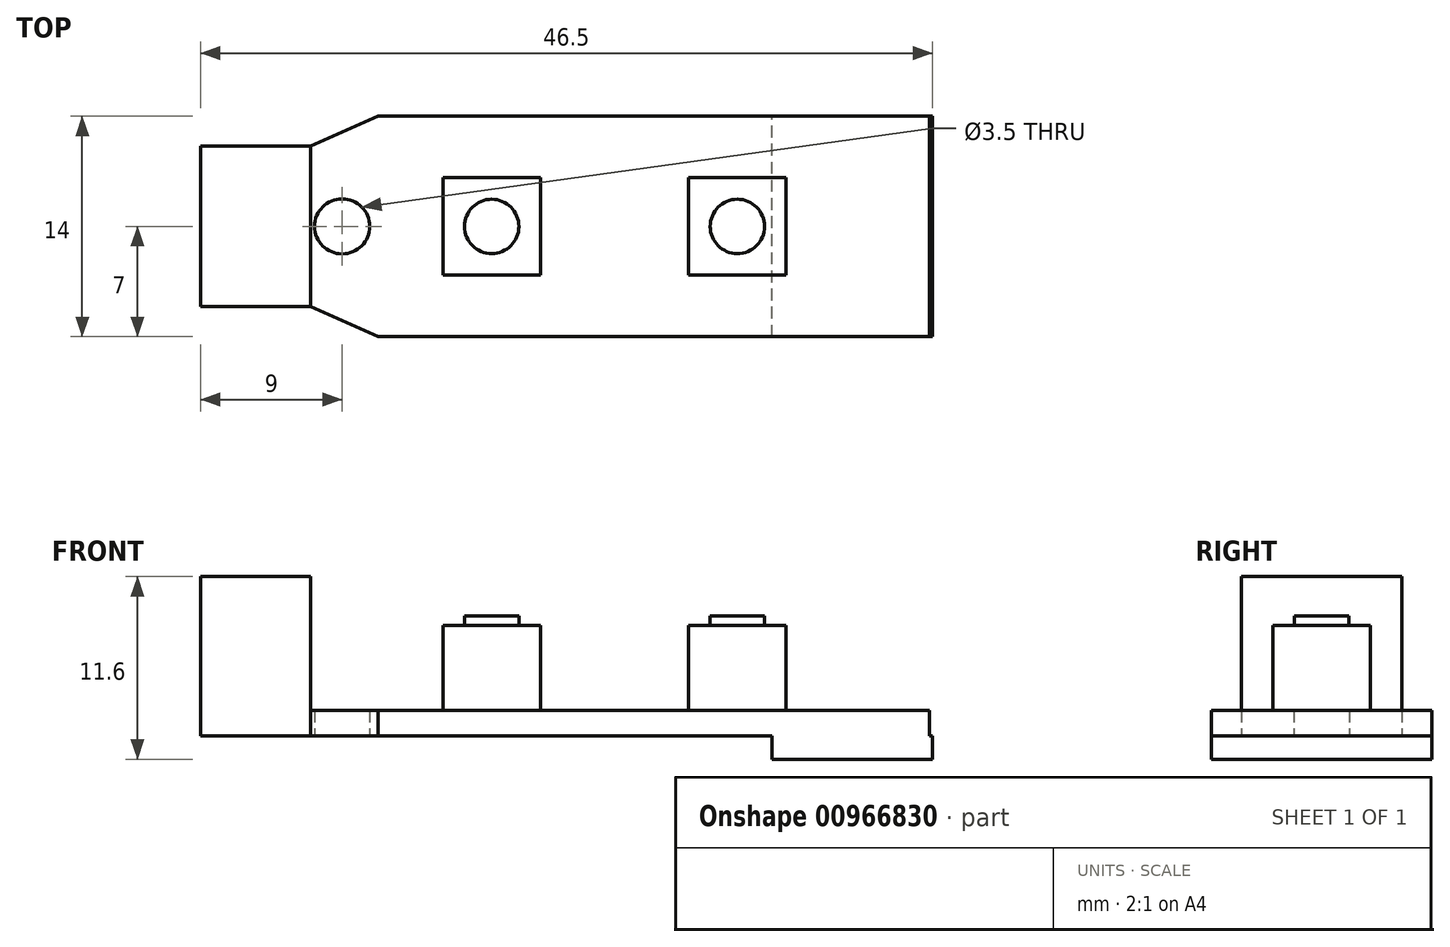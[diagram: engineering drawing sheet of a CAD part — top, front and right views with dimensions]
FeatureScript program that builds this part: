
annotation { "Feature Type Name" : "Feature", "Feature Type Description" : "" }
export const myFeature = defineFeature(function(context is Context, id is Id, definition is map)
    precondition{}
    {
        {
            var Q0;
            Q0=qCreatedBy(makeId("Top.planeOp"),FACE);
            var sketch = newSketch(context, id + "F0", { "sketchPlane" : qUnion([Q0])});
            skLineSegment(sketch, "E0.left", {"start": v(-23.15, 5.1) * mm, "end": v(-23.15, -5.1) * mm});
            skLineSegment(sketch, "E0.right", {"start": v(23.15, 7) * mm, "end": v(23.15, -7) * mm});
            skCircle(sketch, "E1", {"center": v(-14.15, 0) * mm, "radius": 1.75 * mm});
            skLineSegment(sketch, "E2", {"start": v(23.15, 7) * mm, "end": v(-11.85, 7) * mm});
            skLineSegment(sketch, "E3", {"start": v(23.15, -7) * mm, "end": v(-11.85, -7) * mm});
            skLineSegment(sketch, "E4", {"start": v(-23.15, 5.1) * mm, "end": v(-16.15, 5.1) * mm});
            skLineSegment(sketch, "E5", {"start": v(-23.15, -5.1) * mm, "end": v(-16.15, -5.1) * mm});
            skLineSegment(sketch, "E6", {"start": v(-16.15, 5.1) * mm, "end": v(-11.85, 7) * mm});
            skLineSegment(sketch, "E7", {"start": v(-16.15, -5.1) * mm, "end": v(-11.85, -7) * mm});
            skSolve(sketch);
        }
        {
            var Q0;
            Q0 = qSketchRegion(id + "F0", true);
            extrude(context, id + "F1", {"entities" : qUnion([Q0]), "depth" : 1.6 * mm, "offsetDistance" : 25 * mm});
        }
        {
            var Q0;
            Q0=makeQuery(id+"F1.opExtrude","CAP_FACE",FACE,{"disambiguationData":[OSD([sQuery(id+"F0.wireOp",EDGE,"E0.bottom"),sQuery(id+"F0.wireOp",EDGE,"E0.top"),sQuery(id+"F0.wireOp",EDGE,"E0.left"),sQuery(id+"F0.wireOp",EDGE,"E0.right"),sQuery(id+"F0.wireOp",EDGE,"E1")])],"isStart":false});
            var sketch = newSketch(context, id + "F2", { "sketchPlane" : qUnion([Q0])});
            skLineSegment(sketch, "E8.bottom", {"start": v(-23.15, 5.1) * mm, "end": v(-16.15, 5.1) * mm});
            skLineSegment(sketch, "E8.top", {"start": v(-23.15, -5.1) * mm, "end": v(-16.15, -5.1) * mm});
            skLineSegment(sketch, "E8.left", {"start": v(-23.15, 5.1) * mm, "end": v(-23.15, -5.1) * mm});
            skLineSegment(sketch, "E8.right", {"start": v(-16.15, 5.1) * mm, "end": v(-16.15, -5.1) * mm});
            skSolve(sketch);
        }
        {
            var Q0;
            Q0 = qSketchRegion(id + "F2", true);
            extrude(context, id + "F3", {"entities" : qUnion([Q0]), "operationType" : NewBodyOperationType.ADD, "depth" : 8.5 * mm, "offsetDistance" : 25 * mm});
        }
        {
            var Q0;
            Q0=makeQuery(id+"F1.opExtrude","CAP_FACE",FACE,{"disambiguationData":[OSD([sQuery(id+"F0.wireOp",EDGE,"E0.left"),sQuery(id+"F0.wireOp",EDGE,"E0.right"),sQuery(id+"F0.wireOp",EDGE,"E1"),sQuery(id+"F0.wireOp",EDGE,"E2"),sQuery(id+"F0.wireOp",EDGE,"E3"),sQuery(id+"F0.wireOp",EDGE,"JauPMEDd-Xxf6-qXM7-ZYm1-RprdkEthULBr"),sQuery(id+"F0.wireOp",EDGE,"BpJjFPcN-h0H7-t4R9-BkB2-neei3DgV5vJw")])],"isStart":false});
            var sketch = newSketch(context, id + "F4", { "sketchPlane" : qUnion([Q0])});
            skLineSegment(sketch, "E9.bottom", {"start": v(-7.75, 3.1) * mm, "end": v(-1.55, 3.1) * mm});
            skLineSegment(sketch, "E9.top", {"start": v(-7.75, -3.1) * mm, "end": v(-1.55, -3.1) * mm});
            skLineSegment(sketch, "E9.left", {"start": v(-7.75, 3.1) * mm, "end": v(-7.75, -3.1) * mm});
            skLineSegment(sketch, "E9.right", {"start": v(-1.55, 3.1) * mm, "end": v(-1.55, -3.1) * mm});
            skLineSegment(sketch, "E10.bottom", {"start": v(7.85, 3.1) * mm, "end": v(14.05, 3.1) * mm});
            skLineSegment(sketch, "E10.top", {"start": v(7.85, -3.1) * mm, "end": v(14.05, -3.1) * mm});
            skLineSegment(sketch, "E10.left", {"start": v(7.85, 3.1) * mm, "end": v(7.85, -3.1) * mm});
            skLineSegment(sketch, "E10.right", {"start": v(14.05, 3.1) * mm, "end": v(14.05, -3.1) * mm});
            skSolve(sketch);
        }
        {
            var Q0;
            Q0 = qSketchRegion(id + "F4", true);
            extrude(context, id + "F5", {"entities" : qUnion([Q0]), "operationType" : NewBodyOperationType.ADD, "depth" : 5.4 * mm, "offsetDistance" : 25 * mm});
        }
        {
            var Q0;
            Q0=makeQuery(id+"F5.opExtrude","CAP_FACE",FACE,{"disambiguationData":[OSD([sQuery(id+"F4.wireOp",EDGE,"E9.bottom"),sQuery(id+"F4.wireOp",EDGE,"E9.top"),sQuery(id+"F4.wireOp",EDGE,"E9.left"),sQuery(id+"F4.wireOp",EDGE,"E9.right")])],"isStart":false});
            var sketch = newSketch(context, id + "F6", { "sketchPlane" : qUnion([Q0])});
            skCircle(sketch, "E11", {"center": v(-4.65, 0) * mm, "radius": 1.73 * mm});
            skPoint(sketch, "E11.centerSnap0", {"position": v(-4.65, 3.1) * mm});
            skPoint(sketch, "E11.centerSnap1", {"position": v(-7.75, 0) * mm});
            skSolve(sketch);
        }
        {
            var Q0;
            Q0=makeQuery(id+"F5.opExtrude","CAP_FACE",FACE,{"disambiguationData":[OSD([sQuery(id+"F4.wireOp",EDGE,"E10.bottom"),sQuery(id+"F4.wireOp",EDGE,"E10.top"),sQuery(id+"F4.wireOp",EDGE,"E10.left"),sQuery(id+"F4.wireOp",EDGE,"E10.right")])],"isStart":false});
            var sketch = newSketch(context, id + "F7", { "sketchPlane" : qUnion([Q0])});
            skCircle(sketch, "E12", {"center": v(10.95, 0) * mm, "radius": 1.73 * mm});
            skPoint(sketch, "E12.centerSnap0", {"position": v(10.95, 3.1) * mm});
            skSolve(sketch);
        }
        {
            var Q0;
            Q0 = qSketchRegion(id + "F6", true);
            var Q1;
            Q1=makeQuery(id+"F7.imprint","IMPRINT",FACE,{"disambiguationData":[TD([[makeQuery(id+"F7.imprint","IMPRINT",EDGE,{"derivedFrom":sQuery(id+"F7.wireOp",EDGE,"E12")}),1.0]])]});
            extrude(context, id + "F8", {"entities" : qUnion([Q0, Q1]), "operationType" : NewBodyOperationType.ADD, "depth" : 0.6 * mm, "offsetDistance" : 25 * mm});
        }
        {
            var Q0;
            Q0=makeQuery(id+"F1.opExtrude","CAP_FACE",FACE,{"disambiguationData":[OSD([sQuery(id+"F0.wireOp",EDGE,"E0.left"),sQuery(id+"F0.wireOp",EDGE,"E0.right"),sQuery(id+"F0.wireOp",EDGE,"E1"),sQuery(id+"F0.wireOp",EDGE,"E2"),sQuery(id+"F0.wireOp",EDGE,"E3"),sQuery(id+"F0.wireOp",EDGE,"E4"),sQuery(id+"F0.wireOp",EDGE,"E5"),sQuery(id+"F0.wireOp",EDGE,"E6"),sQuery(id+"F0.wireOp",EDGE,"E7")])],"isStart":true});
            var sketch = newSketch(context, id + "F9", { "sketchPlane" : qUnion([Q0])});
            skLineSegment(sketch, "E13.bottom", {"start": v(23.15, 7) * mm, "end": v(13.15, 7) * mm});
            skLineSegment(sketch, "E13.top", {"start": v(23.15, -7) * mm, "end": v(13.15, -7) * mm});
            skLineSegment(sketch, "E13.right", {"start": v(13.15, 7) * mm, "end": v(13.15, -7) * mm});
            skLineSegment(sketch, "E14.bottom", {"start": v(23.15, 7) * mm, "end": v(23.35, 7) * mm});
            skLineSegment(sketch, "E14.top", {"start": v(23.15, -7) * mm, "end": v(23.35, -7) * mm});
            skLineSegment(sketch, "E14.right", {"start": v(23.35, 7) * mm, "end": v(23.35, -7) * mm});
            skLineSegment(sketch, "E15", {"start": v(13.15, 7) * mm, "end": v(23.15, 7) * mm});
            skSolve(sketch);
        }
        {
            var Q0;
            Q0 = qSketchRegion(id + "F9", true);
            extrude(context, id + "F10", {"entities" : qUnion([Q0]), "operationType" : NewBodyOperationType.ADD, "depth" : 1.5 * mm, "offsetDistance" : 25 * mm});
        }
    });
